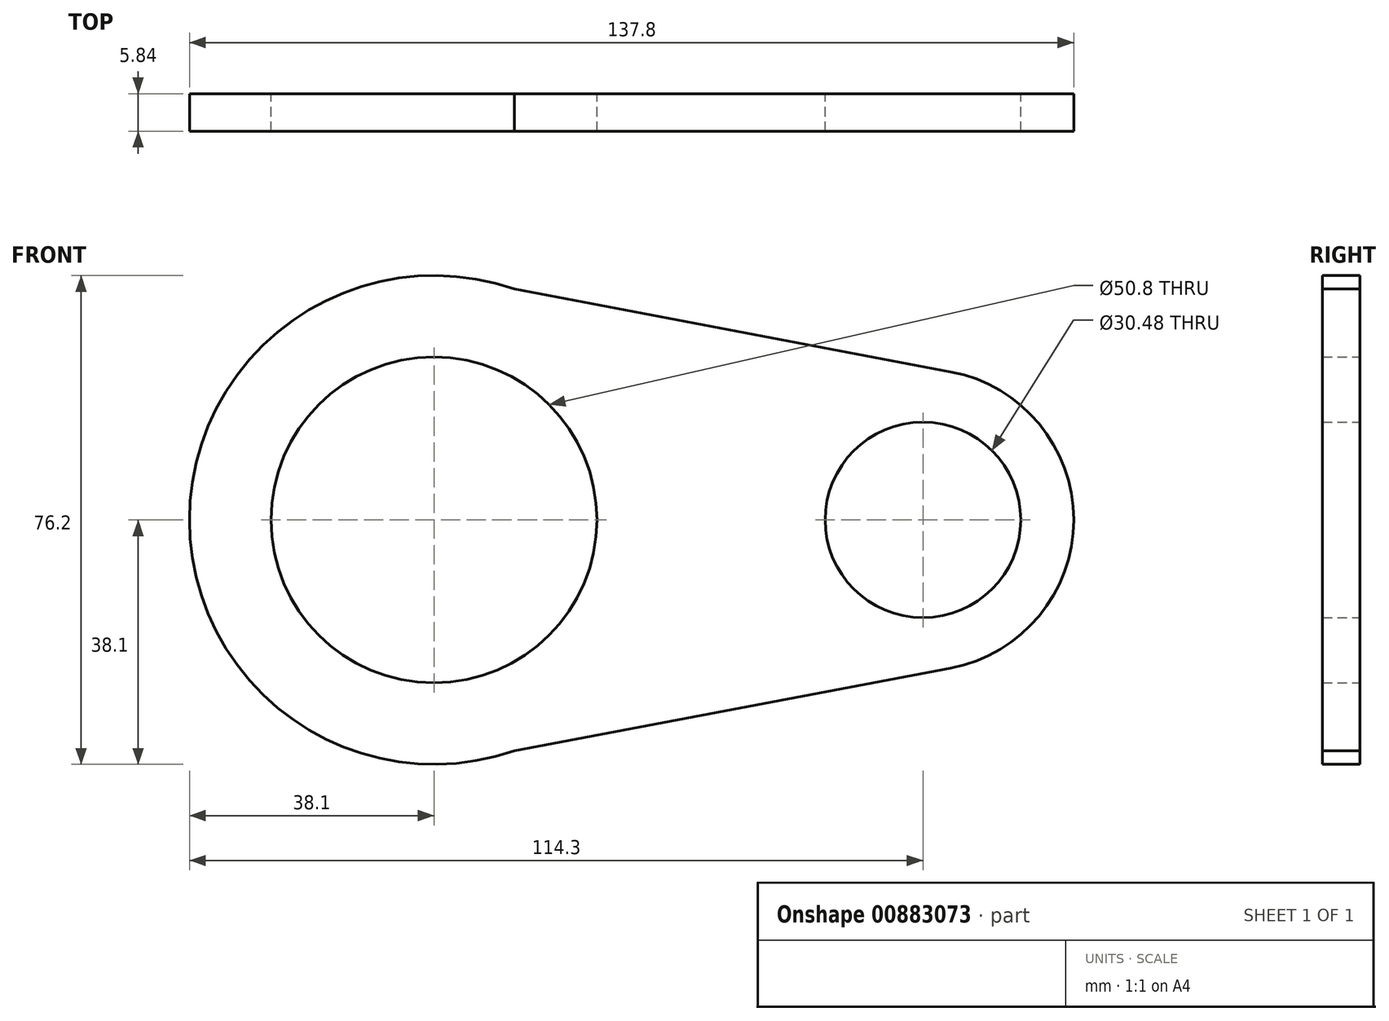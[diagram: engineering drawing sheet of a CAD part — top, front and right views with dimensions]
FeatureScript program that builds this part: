
annotation { "Feature Type Name" : "Feature", "Feature Type Description" : "" }
export const myFeature = defineFeature(function(context is Context, id is Id, definition is map)
    precondition{}
    {
        {
            var Q0;
            Q0=qCreatedBy(makeId("Front.planeOp"),FACE);
            var sketch = newSketch(context, id + "F0", { "sketchPlane" : qUnion([Q0])});
            skArc(sketch, "E0", {"start": v(-64.42, 35.99) * mm, "mid": v(-115.03, 0) * mm, "end": v(-64.42, -35.99) * mm});
            skArc(sketch, "E1", {"start": v(3.65, -23.08) * mm, "mid": v(22.77, 0) * mm, "end": v(3.65, 23.08) * mm});
            skLineSegment(sketch, "E2", {"start": v(-75.4, 38.07) * mm, "end": v(3.65, 23.08) * mm});
            skLineSegment(sketch, "E3", {"start": v(-75.4, -38.07) * mm, "end": v(3.65, -23.08) * mm});
            skCircle(sketch, "E4", {"center": v(-76.93, 0) * mm, "radius": 25.4 * mm});
            skCircle(sketch, "E5", {"center": v(-0.73, 0) * mm, "radius": 15.24 * mm});
            skSolve(sketch);
        }
        {
            var Q0;
            Q0 = qSketchRegion(id + "F0", true);
            extrude(context, id + "F1", {"entities" : qUnion([Q0]), "depth" : 5.6 * mm, "offsetDistance" : 25.4 * mm});
        }
        {
            var Q0;
            Q0 = qSketchRegion(id + "F0", true);
            extrude(context, id + "F2", {"entities" : qUnion([Q0]), "operationType" : NewBodyOperationType.ADD, "depth" : 5.84 * mm, "offsetDistance" : 25.4 * mm});
        }
    });
